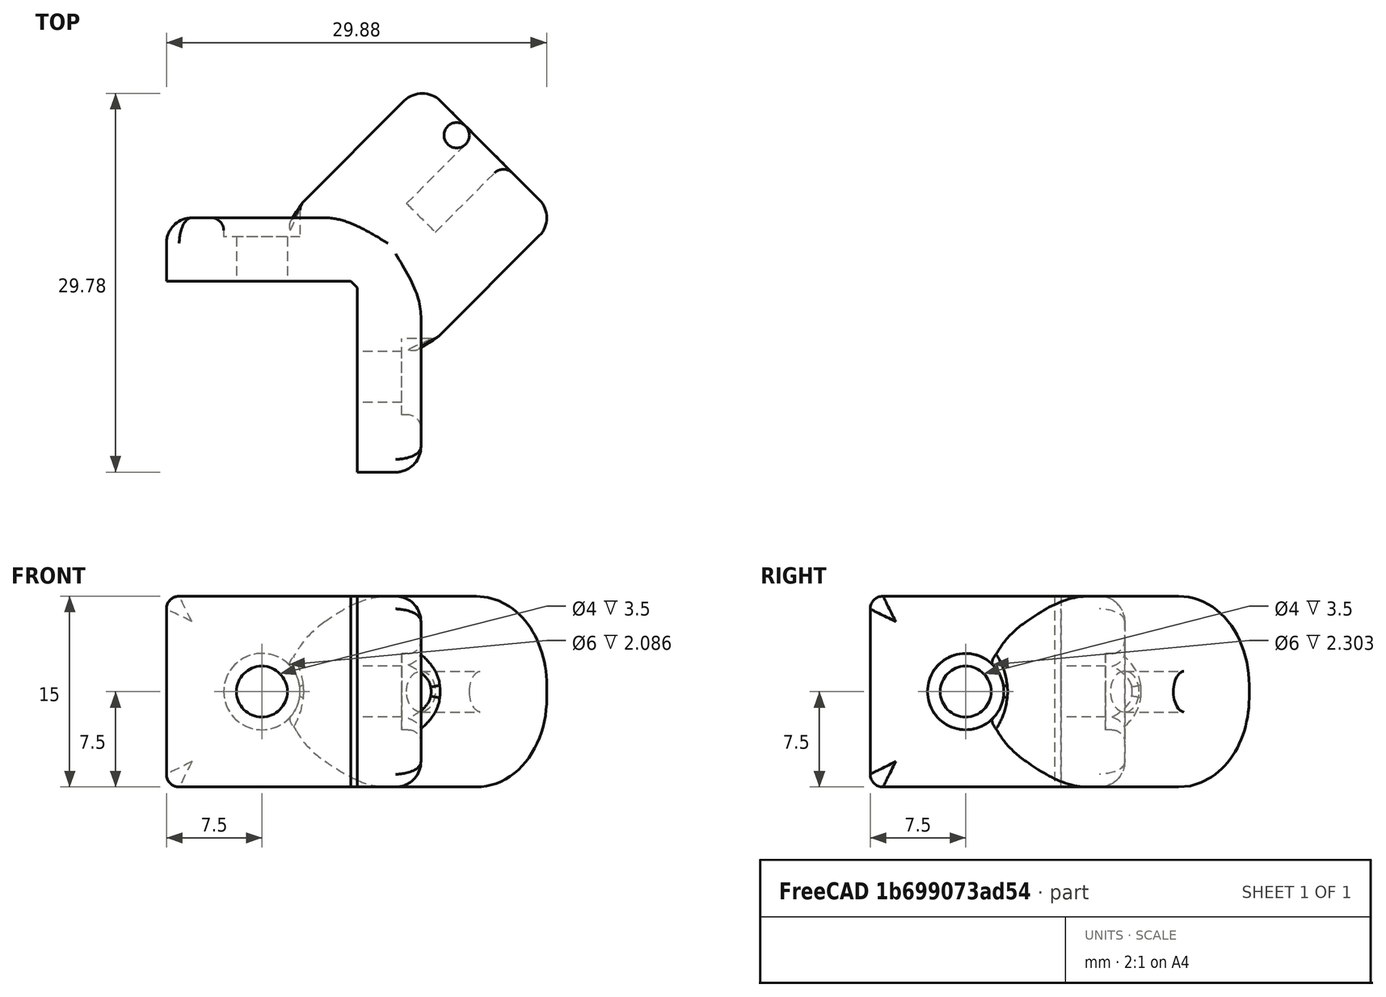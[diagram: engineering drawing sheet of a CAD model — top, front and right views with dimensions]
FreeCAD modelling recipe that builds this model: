
FCSTD DOCUMENT  (FreeCAD 0.14R3703 (Git))
Label: GOUM_45er_2
License: CC-BY 3.0
LicenseURL: http://creativecommons.org/licenses/by/3.0/
objects: Part::Fillet×10, Part::Cylinder×5, Part::Box×3, Part::MultiFuse×3, Part::Cut×3
note: 24 computed .brp shape members not serialized (recipe doc carries the construction recipe); baked Part::Feature solids carry a one-line shape summary decoded from their .brp

FEATURE [Part::Box] Box  label="Cube"
  Height = 5
  Length = 15
  Width = 15
FEATURE [Part::Box] Box001  label="Cube001"
  Height = 20
  Length = 5
  Placement = pos=(15,0,0) rot=(0,0,1;0rad)
  Width = 15
FEATURE [Part::Cylinder] Cylinder
  Angle = 360
  Height = 10
  Placement = pos=(7.5,7.5,-8.5) rot=(0,0,1;0rad)
  Radius = 3
FEATURE [Part::Cylinder] Cylinder001
  Angle = 360
  Height = 10
  Placement = pos=(7.5,7.5,0) rot=(0,0,1;0rad)
  Radius = 2
FEATURE [Part::Cylinder] Cylinder002
  Angle = 360
  Height = 10
  Placement = pos=(0,0,-8.5) rot=(0,0,1;0rad)
  Radius = 3
FEATURE [Part::Cylinder] Cylinder003
  Angle = 360
  Height = 10
  Radius = 2
FEATURE [Part::MultiFuse] Fusion
  Shapes = -> [Cylinder,Cylinder001]
FEATURE [Part::MultiFuse] Fusion001
  Placement = pos=(20,7.5,12.5) rot=(0,-1,0;1.5708rad)
  Shapes = -> [Cylinder002,Cylinder003]
FEATURE [Part::Box] Box002  label="Cube002"
  Height = 15
  Length = 15
  Placement = pos=(9.5,0,0) rot=(0,1,0;0.785398rad)
  Width = 15
FEATURE [Part::Cylinder] Cylinder004
  Angle = 360
  Height = 10
  Placement = pos=(20,7.5,0) rot=(0,1,0;2.35619rad)
  Radius = 1.6
FEATURE [Part::Fillet] Fillet
  Base = -> Box002
  Edges = 4 edges r=7: [Edge9,Edge10,Edge11,Edge12]
FEATURE [Part::Fillet] Fillet001
  Base = -> Fillet
  Edges = 8 edges r=2: [Edge9,Edge13,Edge15,Edge17,Edge19,Edge21,Edge23,Edge24]
FEATURE [Part::Fillet] Fillet002
  Base = -> Box001
  Edges = 3 edges r=2: [Edge5,Edge6,Edge7]
FEATURE [Part::Fillet] Fillet003
  Base = -> Box
  Edges = 3 edges r=2: [Edge4,Edge9,Edge11]
FEATURE [Part::Fillet] Fillet004
  Base = -> Fillet002
  Edges = 2 edges r=2: [Edge5,Edge8]
FEATURE [Part::Cut] Cut
  Base = -> Fillet001
  Tool = -> Cylinder004
FEATURE [Part::Fillet] Fillet005
  Base = -> Cut
  Edges = 1 edges r=1: [Edge29]
FEATURE [Part::MultiFuse] Fusion002
  Shapes = -> [Fillet005,Fillet003,Fillet004]
FEATURE [Part::Cut] Cut001
  Base = -> Fusion002
  Tool = -> Fusion001
FEATURE [Part::Cut] Cut002
  Base = -> Cut001
  Tool = -> Fusion
FEATURE [Part::Fillet] Fillet006
  Base = -> Cut002
  Edges = 5 edges r=1: [Edge35,Edge43,Edge44,Edge49,Edge65]
FEATURE [Part::Fillet] Fillet007
  Base = -> Fillet006
  Edges = 5 edges r=1: [Edge59,Edge90,Edge93,Edge94,Edge95]
  Placement = pos=(0,0,0) rot=(1,0,0;1.5708rad)
FEATURE [Part::Fillet] Fillet008
  Base = -> Fillet007
  Edges = 2 edges r=1: [Edge68,Edge106]
FEATURE [Part::Fillet] Fillet009  label="Filament-support-45-deg"
  Base = -> Fillet008
  Edges = 2 edges r=1: [Edge103,Edge139]
